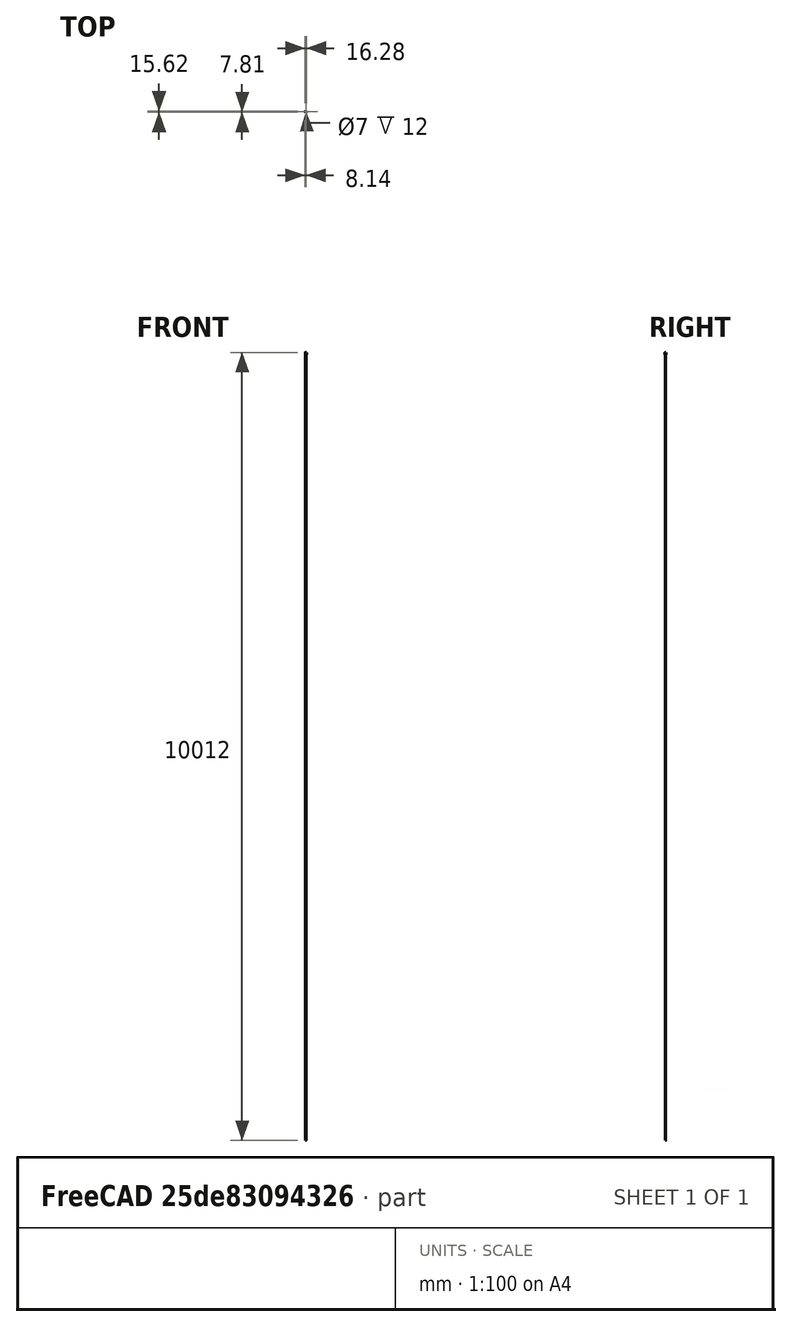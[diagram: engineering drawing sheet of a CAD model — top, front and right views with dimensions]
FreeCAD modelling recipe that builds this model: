
FCSTD DOCUMENT  (FreeCAD 0.16R)
Label: StudCondoms
License: All rights reserved
LicenseURL: http://en.wikipedia.org/wiki/All_rights_reserved
objects: Sketcher::SketchObject×5, PartDesign::Pocket×3, PartDesign::Pad×2, Mesh::Feature×1
note: 15 computed .brp shape members not serialized (recipe doc carries the construction recipe); baked Part::Feature solids carry a one-line shape summary decoded from their .brp

FEATURE [Sketcher::SketchObject] Sketch
  sketch-geometry (1):
    g0: Circle CenterX=0 CenterY=0 CenterZ=0 NormalX=0 NormalY=0 NormalZ=1 Radius=6
  constraints (2):
    c: Coincident(g0,g-1)
    c: Radius(g0) = 6
FEATURE [PartDesign::Pad] Pad
  Length = 25
  Length2 = 100
  Sketch = -> Sketch
  Type = 0
FEATURE [Sketcher::SketchObject] Sketch001
  Placement = pos=(0,0,25) rot=(0,0,1;0rad)
  Support = -> Pad [Face3]
  sketch-geometry (1):
    g0: Circle CenterX=0 CenterY=0 CenterZ=0 NormalX=0 NormalY=0 NormalZ=1 Radius=3.5
  constraints (2):
    c: Coincident(g0,g-1)
    c: Radius(g0) = 3.5
FEATURE [PartDesign::Pocket] Pocket
  Length = 12
  Sketch = -> Sketch001
  Type = 0
FEATURE [Sketcher::SketchObject] Sketch002
  Placement = pos=(0,0,13) rot=(0,0,1;0rad)
  Support = -> Pocket [Face5]
  sketch-geometry (1):
    g0: Circle CenterX=0 CenterY=0 CenterZ=0 NormalX=0 NormalY=0 NormalZ=1 Radius=1.9
  constraints (2):
    c: Coincident(g0,g-1)
    c: Radius(g0) = 1.9
FEATURE [PartDesign::Pocket] Pocket001
  Length = 5
  Sketch = -> Sketch002
  Type = 1
FEATURE [Sketcher::SketchObject] Sketch003
  Placement = pos=(0,0,13) rot=(0,0,1;0rad)
  Support = -> Pocket001 [Face6]
  sketch-geometry (7):
    g0: LineSegment StartX=0.448867 StartY=-2.10504 StartZ=0 EndX=2.04745 EndY=-0.66379 EndZ=0
    g1: LineSegment StartX=2.04745 StartY=-0.66379 StartZ=0 EndX=1.59858 EndY=1.44125 EndZ=0
    g2: LineSegment StartX=1.59858 StartY=1.44125 StartZ=0 EndX=-0.448867 EndY=2.10504 EndZ=0
    g3: LineSegment StartX=-0.448867 StartY=2.10504 StartZ=0 EndX=-2.04745 EndY=0.66379 EndZ=0
    g4: LineSegment StartX=-2.04745 StartY=0.66379 StartZ=0 EndX=-1.59858 EndY=-1.44125 EndZ=0
    g5: LineSegment StartX=-1.59858 StartY=-1.44125 StartZ=0 EndX=0.448867 EndY=-2.10504 EndZ=0
    g6: Circle [constr] CenterX=0 CenterY=0 CenterZ=0 NormalX=0 NormalY=0 NormalZ=1 Radius=2.15237
  constraints (14):
    c: Coincident(g0,g1)
    c: Coincident(g1,g2)
    c: Coincident(g2,g3)
    c: Coincident(g3,g4)
    c: Coincident(g4,g5)
    c: Coincident(g5,g0)
    c: Equal(g0, g1-g5) x5
    c: PointOnObject(g0,g6)
    c: PointOnObject(g1,g6)
    c: PointOnObject(g2,g6)
    c: PointOnObject(g3,g6)
    c: PointOnObject(g4,g6)
    c: PointOnObject(g5,g6)
    c: Coincident(g6,g-1)
FEATURE [PartDesign::Pocket] Pocket002
  Length = 5
  Sketch = -> Sketch003
  Type = 1
FEATURE [Sketcher::SketchObject] Sketch004
  Placement = pos=(0,0,0) rot=(1,0,0;3.14159rad)
  Support = -> Pocket002 [Face2]
  sketch-geometry (7):
    g0: LineSegment StartX=5.38202 StartY=-6.28951 StartZ=0 EndX=8.13789 EndY=1.51621 EndZ=0
    g1: LineSegment StartX=8.13789 StartY=1.51621 StartZ=0 EndX=2.75587 EndY=7.80572 EndZ=0
    g2: LineSegment StartX=2.75587 StartY=7.80572 StartZ=0 EndX=-5.38202 EndY=6.28951 EndZ=0
    g3: LineSegment StartX=-5.38202 StartY=6.28951 StartZ=0 EndX=-8.13789 EndY=-1.51621 EndZ=0
    g4: LineSegment StartX=-8.13789 StartY=-1.51621 StartZ=0 EndX=-2.75587 EndY=-7.80572 EndZ=0
    g5: LineSegment StartX=-2.75587 StartY=-7.80572 StartZ=0 EndX=5.38202 EndY=-6.28951 EndZ=0
    g6: Circle [constr] CenterX=0 CenterY=0 CenterZ=0 NormalX=0 NormalY=0 NormalZ=1 Radius=8.27793
  constraints (14):
    c: Coincident(g0,g1)
    c: Coincident(g1,g2)
    c: Coincident(g2,g3)
    c: Coincident(g3,g4)
    c: Coincident(g4,g5)
    c: Coincident(g5,g0)
    c: Equal(g0, g1-g5) x5
    c: PointOnObject(g0,g6)
    c: PointOnObject(g1,g6)
    c: PointOnObject(g2,g6)
    c: PointOnObject(g3,g6)
    c: PointOnObject(g4,g6)
    c: PointOnObject(g5,g6)
    c: Coincident(g6,g-1)
FEATURE [PartDesign::Pad] Pad001
  Length = 5
  Length2 = 100
  Sketch = -> Sketch004
  Type = 0
FEATURE [Mesh::Feature] Mesh  label="Pad001 (Meshed)"
